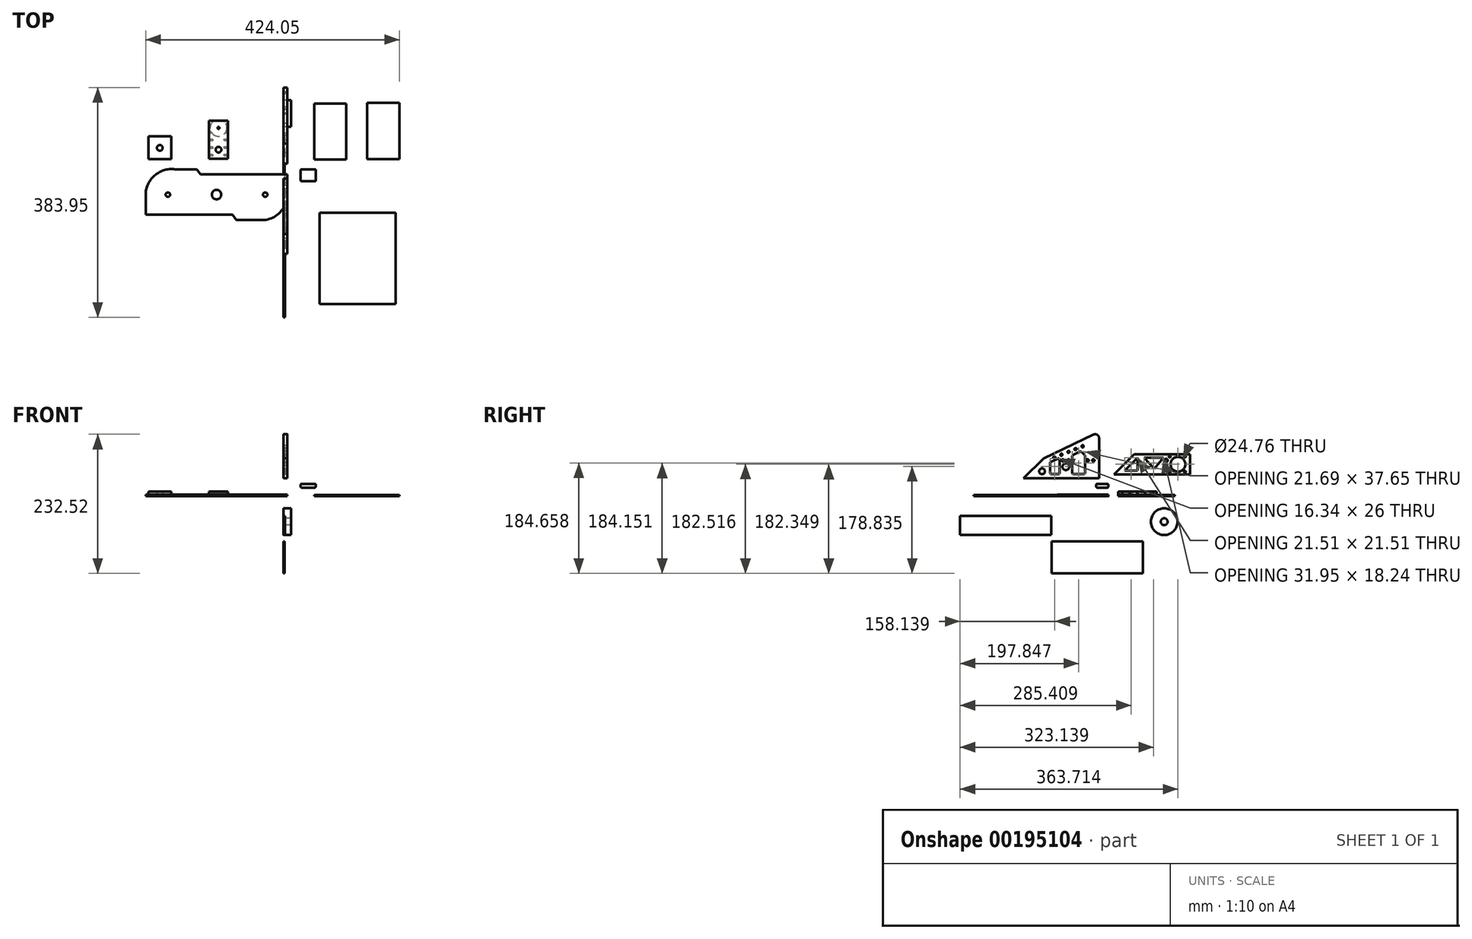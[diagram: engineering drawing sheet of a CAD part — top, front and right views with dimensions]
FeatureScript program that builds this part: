
annotation { "Feature Type Name" : "Feature", "Feature Type Description" : "" }
export const myFeature = defineFeature(function(context is Context, id is Id, definition is map)
    precondition{}
    {
        {
            var Q0;
            Q0=qCreatedBy(makeId("Top.planeOp"),FACE);
            var sketch = newSketch(context, id + "F0", { "sketchPlane" : qUnion([Q0])});
            skLineSegment(sketch, "E0.bottom", {"start": v(-85.5, -8.64) * mm, "end": v(-138.32, -8.64) * mm});
            skLineSegment(sketch, "E0.top", {"start": v(-85.5, -75.95) * mm, "end": v(-138.32, -75.95) * mm});
            skPoint(sketch, "E0.middle", {"position": v(-111.9, -42.3) * mm});
            skLineSegment(sketch, "E1", {"start": v(-138.32, -8.64) * mm, "end": v(-144.93, 0) * mm});
            skLineSegment(sketch, "E2", {"start": v(-144.93, 0) * mm, "end": v(-181.5, 0) * mm});
            skLineSegment(sketch, "E3", {"start": v(-181.5, -75.95) * mm, "end": v(-230.27, -75.95) * mm});
            skLineSegment(sketch, "E4", {"start": v(-230.27, -75.95) * mm, "end": v(-230.27, -42.93) * mm});
            skArc(sketch, "E5", {"start": v(-181.5, 0) * mm, "mid": v(-215.59, -10.44) * mm, "end": v(-230.27, -42.93) * mm});
            skLineSegment(sketch, "E6", {"start": v(-111.9, -42.3) * mm, "end": v(-100.72, -42.3) * mm});
            skLineSegment(sketch, "E7", {"start": v(-111.9, -42.3) * mm, "end": v(-111.9, -49.73) * mm});
            skLineSegment(sketch, "E8.MirrorCS", {"start": v(-42.31, -8.64) * mm, "end": v(6.46, -8.64) * mm});
            skLineSegment(sketch, "E9.MirrorCS", {"start": v(6.46, -8.64) * mm, "end": v(6.46, -41.66) * mm});
            skArc(sketch, "E10.MirrorCS", {"start": v(-42.31, -84.58) * mm, "mid": v(-8.23, -74.14) * mm, "end": v(6.46, -41.66) * mm});
            skLineSegment(sketch, "E11.MirrorCS", {"start": v(-78.89, -84.58) * mm, "end": v(-42.31, -84.58) * mm});
            skLineSegment(sketch, "E12.MirrorCS", {"start": v(-85.5, -75.95) * mm, "end": v(-78.89, -84.58) * mm});
            skLineSegment(sketch, "E13", {"start": v(-42.31, -8.64) * mm, "end": v(-85.5, -8.64) * mm});
            skLineSegment(sketch, "E14", {"start": v(-181.5, -75.95) * mm, "end": v(-138.32, -75.95) * mm});
            skCircle(sketch, "E15", {"center": v(-111.9, -42.3) * mm, "radius": 7.87 * mm});
            skCircle(sketch, "E16", {"center": v(-193.19, -42.3) * mm, "radius": 3.68 * mm});
            skCircle(sketch, "E17.MirrorC", {"center": v(-30.63, -42.3) * mm, "radius": 3.68 * mm});
            skSolve(sketch);
        }
        {
            var Q0;
            Q0 = qSketchRegion(id + "F0", true);
            extrude(context, id + "F1", {"entities" : qUnion([Q0]), "depth" : 3.05 * mm});
        }
        {
            var Q0;
            Q0=qCreatedBy(makeId("Top.planeOp"),FACE);
            var sketch = newSketch(context, id + "F2", { "sketchPlane" : qUnion([Q0])});
            skLineSegment(sketch, "E18.bottom", {"start": v(-187.63, 16.69) * mm, "end": v(-225.73, 16.69) * mm});
            skLineSegment(sketch, "E18.top", {"start": v(-187.63, 54.79) * mm, "end": v(-225.73, 54.79) * mm});
            skLineSegment(sketch, "E18.left", {"start": v(-187.63, 16.69) * mm, "end": v(-187.63, 54.79) * mm});
            skLineSegment(sketch, "E18.right", {"start": v(-225.73, 16.69) * mm, "end": v(-225.73, 54.79) * mm});
            skCircle(sketch, "E19", {"center": v(-206.68, 35.74) * mm, "radius": 4.76 * mm});
            skPoint(sketch, "E19.centerSnap0", {"position": v(-206.68, 54.79) * mm});
            skPoint(sketch, "E19.centerSnap1", {"position": v(-187.63, 35.74) * mm});
            skSolve(sketch);
        }
        {
            var Q0;
            Q0 = qSketchRegion(id + "F2", true);
            extrude(context, id + "F3", {"entities" : qUnion([Q0]), "depth" : 7.94 * mm});
        }
        {
            var Q0;
            Q0=qCreatedBy(makeId("Right.planeOp"),FACE);
            var sketch = newSketch(context, id + "F4", { "sketchPlane" : qUnion([Q0])});
            skLineSegment(sketch, "E20", {"start": v(-108.08, 63.04) * mm, "end": v(-24.5, 102.95) * mm});
            skLineSegment(sketch, "E21", {"start": v(-15.41, 97.22) * mm, "end": v(-15.41, 29.83) * mm});
            skLineSegment(sketch, "E22", {"start": v(-15.41, 29.83) * mm, "end": v(-106.33, 29.83) * mm});
            skLineSegment(sketch, "E23", {"start": v(-97.35, 54.98) * mm, "end": v(-97.35, 39.42) * mm});
            skLineSegment(sketch, "E24", {"start": v(-94.81, 36.88) * mm, "end": v(-83.55, 36.88) * mm});
            skLineSegment(sketch, "E25", {"start": v(-81.01, 39.42) * mm, "end": v(-81.01, 60.35) * mm});
            skLineSegment(sketch, "E26", {"start": v(-84.65, 62.64) * mm, "end": v(-95.9, 57.27) * mm});
            skCircle(sketch, "E27", {"center": v(-70.88, 49.3) * mm, "radius": 5.61 * mm});
            skLineSegment(sketch, "E28.direction1", {"start": v(-70.88, 49.3) * mm, "end": v(-43.02, 60.8) * mm, "construction": true});
            skLineSegment(sketch, "E28.direction2", {"start": v(-70.88, 49.3) * mm, "end": v(-70.88, 30.25) * mm, "construction": true});
            skLineSegment(sketch, "E29", {"start": v(-60.32, 66.48) * mm, "end": v(-60.32, 39.42) * mm});
            skLineSegment(sketch, "E30", {"start": v(-57.78, 36.88) * mm, "end": v(-41.17, 36.88) * mm});
            skLineSegment(sketch, "E31", {"start": v(-38.63, 39.42) * mm, "end": v(-38.63, 67.02) * mm});
            skLineSegment(sketch, "E32", {"start": v(-39.39, 68.83) * mm, "end": v(-44.45, 73.8) * mm});
            skLineSegment(sketch, "E33", {"start": v(-47.32, 74.28) * mm, "end": v(-58.87, 68.77) * mm});
            skLineSegment(sketch, "E34", {"start": v(-106.33, 29.83) * mm, "end": v(-141.28, 29.83) * mm});
            skLineSegment(sketch, "E35", {"start": v(-141.28, 29.83) * mm, "end": v(-108.08, 63.04) * mm});
            skCircle(sketch, "E36", {"center": v(-110.57, 41.64) * mm, "radius": 4.84 * mm});
            skPoint(sketch, "E37.visualSharp", {"position": v(-15.41, 107.28) * mm});
            skArc(sketch, "E37.filletArc", {"start": v(-15.41, 97.22) * mm, "mid": v(-18.37, 102.59) * mm, "end": v(-24.5, 102.95) * mm});
            skPoint(sketch, "E38.visualSharp", {"position": v(-45.71, 75.05) * mm});
            skArc(sketch, "E38.filletArc", {"start": v(-44.45, 73.8) * mm, "mid": v(-45.8, 74.5) * mm, "end": v(-47.32, 74.28) * mm});
            skPoint(sketch, "E39.visualSharp", {"position": v(-60.32, 68.08) * mm});
            skArc(sketch, "E39.filletArc", {"start": v(-58.87, 68.77) * mm, "mid": v(-59.92, 67.83) * mm, "end": v(-60.32, 66.48) * mm});
            skPoint(sketch, "E40.visualSharp", {"position": v(-38.63, 68.08) * mm});
            skArc(sketch, "E40.filletArc", {"start": v(-38.63, 67.02) * mm, "mid": v(-38.83, 68) * mm, "end": v(-39.39, 68.83) * mm});
            skPoint(sketch, "E41.visualSharp", {"position": v(-81.01, 64.38) * mm});
            skArc(sketch, "E41.filletArc", {"start": v(-81.01, 60.35) * mm, "mid": v(-82.2, 62.5) * mm, "end": v(-84.65, 62.64) * mm});
            skPoint(sketch, "E42.visualSharp", {"position": v(-97.35, 56.58) * mm});
            skArc(sketch, "E42.filletArc", {"start": v(-95.9, 57.27) * mm, "mid": v(-96.96, 56.33) * mm, "end": v(-97.35, 54.98) * mm});
            skPoint(sketch, "E43.visualSharp", {"position": v(-38.63, 36.88) * mm});
            skArc(sketch, "E43.filletArc", {"start": v(-41.17, 36.88) * mm, "mid": v(-39.37, 37.63) * mm, "end": v(-38.63, 39.42) * mm});
            skPoint(sketch, "E44.visualSharp", {"position": v(-60.32, 36.88) * mm});
            skArc(sketch, "E44.filletArc", {"start": v(-60.32, 39.42) * mm, "mid": v(-59.57, 37.63) * mm, "end": v(-57.78, 36.88) * mm});
            skPoint(sketch, "E45.visualSharp", {"position": v(-81.01, 36.88) * mm});
            skArc(sketch, "E45.filletArc", {"start": v(-83.55, 36.88) * mm, "mid": v(-81.76, 37.63) * mm, "end": v(-81.01, 39.42) * mm});
            skPoint(sketch, "E46.visualSharp", {"position": v(-97.35, 36.88) * mm});
            skArc(sketch, "E46.filletArc", {"start": v(-97.35, 39.42) * mm, "mid": v(-96.6, 37.63) * mm, "end": v(-94.81, 36.88) * mm});
            skCircle(sketch, "E47", {"center": v(-75.68, 59.86) * mm, "radius": 1.9 * mm});
            skCircle(sketch, "E48.1.0.0", {"center": v(-66.15, 59.86) * mm, "radius": 1.9 * mm});
            skLineSegment(sketch, "E48.direction1", {"start": v(-75.68, 59.86) * mm, "end": v(-66.15, 59.86) * mm, "construction": true});
            skPoint(sketch, "E49.middle", {"position": v(-70.92, 59.86) * mm});
            skCircle(sketch, "E50", {"center": v(-34.44, 59.86) * mm, "radius": 1.9 * mm});
            skCircle(sketch, "E51.1.0.0", {"center": v(-24.91, 59.86) * mm, "radius": 1.9 * mm});
            skSolve(sketch);
        }
        {
            var Q0;
            Q0 = qSketchRegion(id + "F4", true);
            extrude(context, id + "F5", {"entities" : qUnion([Q0]), "depth" : 6.35 * mm});
        }
        {
            var Q0;
            Q0=qCreatedBy(makeId("Top.planeOp"),FACE);
            var sketch = newSketch(context, id + "F6", { "sketchPlane" : qUnion([Q0])});
            skLineSegment(sketch, "E52.bottom", {"start": v(-124.5, 17.33) * mm, "end": v(-92.76, 17.33) * mm});
            skLineSegment(sketch, "E52.top", {"start": v(-124.5, 80.83) * mm, "end": v(-92.76, 80.83) * mm});
            skLineSegment(sketch, "E52.left", {"start": v(-124.5, 17.33) * mm, "end": v(-124.5, 80.83) * mm});
            skLineSegment(sketch, "E52.right", {"start": v(-92.76, 17.33) * mm, "end": v(-92.76, 80.83) * mm});
            skCircle(sketch, "E53", {"center": v(-108.63, 32.7) * mm, "radius": 4.76 * mm});
            skPoint(sketch, "E53.centerSnap0", {"position": v(-108.63, 17.33) * mm});
            skCircle(sketch, "E54", {"center": v(-108.63, 69.02) * mm, "radius": 1.65 * mm});
            skPoint(sketch, "E54.centerSnap0", {"position": v(-108.63, 80.83) * mm});
            skSolve(sketch);
        }
        {
            var Q0;
            Q0 = qSketchRegion(id + "F6", true);
            extrude(context, id + "F7", {"entities" : qUnion([Q0]), "depth" : 7.94 * mm});
        }
        {
            var Q0;
            Q0=makeQuery(id+"F7.opExtrude","SWEPT_FACE",FACE,{"disambiguationData":[OSD([sQuery(id+"F6.wireOp",EDGE,"E52.right")])]});
            var sketch = newSketch(context, id + "F8", { "sketchPlane" : qUnion([Q0])});
            skCircle(sketch, "E55", {"center": v(23.75, 3.97) * mm, "radius": 1.3 * mm});
            skPoint(sketch, "E55.centerSnap0", {"position": v(17.33, 3.97) * mm});
            skCircle(sketch, "E56.1.0.0", {"center": v(36.45, 3.97) * mm, "radius": 1.3 * mm});
            skCircle(sketch, "E56.2.0.0", {"center": v(49.15, 3.97) * mm, "radius": 1.3 * mm});
            skCircle(sketch, "E56.3.0.0", {"center": v(61.85, 3.97) * mm, "radius": 1.3 * mm});
            skCircle(sketch, "E56.4.0.0", {"center": v(74.55, 3.97) * mm, "radius": 1.3 * mm});
            skLineSegment(sketch, "E56.direction1", {"start": v(23.75, 3.97) * mm, "end": v(36.45, 3.97) * mm, "construction": true});
            skSolve(sketch);
        }
        {
            var Q0;
            Q0 = qSketchRegion(id + "F8", true);
            extrude(context, id + "F9", {"entities" : qUnion([Q0]), "operationType" : NewBodyOperationType.REMOVE, "oppositeDirection" : true, "depth" : 6.35 * mm});
        }
        {
            var Q0;
            Q0=makeQuery(id+"F7.opExtrude","SWEPT_FACE",FACE,{"disambiguationData":[OSD([sQuery(id+"F6.wireOp",EDGE,"E52.left")])]});
            var sketch = newSketch(context, id + "F10", { "sketchPlane" : qUnion([Q0])});
            skCircle(sketch, "E57", {"center": v(-23.1, 3.97) * mm, "radius": 1.36 * mm});
            skPoint(sketch, "E57.centerSnap0", {"position": v(-17.33, 3.97) * mm});
            skCircle(sketch, "E58.1.0.0", {"center": v(-35.8, 3.97) * mm, "radius": 1.36 * mm});
            skCircle(sketch, "E58.2.0.0", {"center": v(-48.5, 3.97) * mm, "radius": 1.36 * mm});
            skCircle(sketch, "E58.3.0.0", {"center": v(-61.2, 3.97) * mm, "radius": 1.36 * mm});
            skCircle(sketch, "E58.4.0.0", {"center": v(-73.9, 3.97) * mm, "radius": 1.36 * mm});
            skLineSegment(sketch, "E58.direction1", {"start": v(-23.1, 3.97) * mm, "end": v(-35.8, 3.97) * mm, "construction": true});
            skSolve(sketch);
        }
        {
            var Q0;
            Q0 = qSketchRegion(id + "F10", true);
            extrude(context, id + "F11", {"entities" : qUnion([Q0]), "operationType" : NewBodyOperationType.REMOVE, "oppositeDirection" : true, "depth" : 6.35 * mm});
        }
        {
            var Q0;
            Q0=makeQuery(id+"F5.opExtrude","CAP_FACE",FACE,{"disambiguationData":[OSD([sQuery(id+"F4.wireOp",EDGE,"hSpsFszO-E8va-vhgR-9E20-GIKQw1AIUSDn"),sQuery(id+"F4.wireOp",EDGE,"E20"),sQuery(id+"F4.wireOp",EDGE,"shNWkFX5-DmJ1-Q3tj-PIuK-kCnUBTTVJkQP"),sQuery(id+"F4.wireOp",EDGE,"E21"),sQuery(id+"F4.wireOp",EDGE,"E22"),sQuery(id+"F4.wireOp",EDGE,"E23"),sQuery(id+"F4.wireOp",EDGE,"E24"),sQuery(id+"F4.wireOp",EDGE,"E25"),sQuery(id+"F4.wireOp",EDGE,"E26"),sQuery(id+"F4.wireOp",EDGE,"E27"),sQuery(id+"F4.wireOp",EDGE,"E28.0.1.0"),sQuery(id+"F4.wireOp",EDGE,"E29"),sQuery(id+"F4.wireOp",EDGE,"E30"),sQuery(id+"F4.wireOp",EDGE,"E31"),sQuery(id+"F4.wireOp",EDGE,"E32"),sQuery(id+"F4.wireOp",EDGE,"E33"),sQuery(id+"F4.wireOp",EDGE,"JjvghidZ-4DsB-nMtc-syiM-kJHiGhE1ZNjx")])],"isStart":false});
            var sketch = newSketch(context, id + "F12", { "sketchPlane" : qUnion([Q0])});
            skCircle(sketch, "E59", {"center": v(-42.83, 83.43) * mm, "radius": 1.78 * mm});
            skCircle(sketch, "E60.1.0.0", {"center": v(-54.64, 78.75) * mm, "radius": 1.78 * mm});
            skCircle(sketch, "E60.2.0.0", {"center": v(-66.44, 74.07) * mm, "radius": 1.78 * mm});
            skCircle(sketch, "E60.3.0.0", {"center": v(-78.25, 69.38) * mm, "radius": 1.78 * mm});
            skCircle(sketch, "E60.4.0.0", {"center": v(-90.05, 64.7) * mm, "radius": 1.78 * mm});
            skLineSegment(sketch, "E60.direction1", {"start": v(-42.83, 83.43) * mm, "end": v(-54.64, 78.75) * mm, "construction": true});
            skSolve(sketch);
        }
        {
            var Q0;
            Q0 = qSketchRegion(id + "F12", true);
            var Q1;
            Q1 = qConstructionFilter(qBodyType(qCreatedBy(id + "F12" ,EDGE), BodyType.WIRE), ConstructionObject.NO);
            extrude(context, id + "F13", {"entities" : qUnion([Q0]), "operationType" : NewBodyOperationType.REMOVE, "surfaceEntities" : qUnion([Q1]), "endBound" : BoundingType.THROUGH_ALL, "oppositeDirection" : true, "depth" : 25.4 * mm});
        }
        {
            var Q0;
            Q0=makeQuery(id+"F7.opExtrude","CAP_FACE",FACE,{"disambiguationData":[OSD([sQuery(id+"F6.wireOp",EDGE,"E52.bottom"),sQuery(id+"F6.wireOp",EDGE,"E52.top"),sQuery(id+"F6.wireOp",EDGE,"E52.left"),sQuery(id+"F6.wireOp",EDGE,"E52.right"),sQuery(id+"F6.wireOp",EDGE,"E53"),sQuery(id+"F6.wireOp",EDGE,"E54")])],"isStart":true});
            var sketch = newSketch(context, id + "F14", { "sketchPlane" : qUnion([Q0])});
            skCircle(sketch, "E61", {"center": v(-108.63, -69.02) * mm, "radius": 14 * mm});
            skSolve(sketch);
        }
        {
            var Q0;
            Q0 = qSketchRegion(id + "F14", true);
            extrude(context, id + "F15", {"entities" : qUnion([Q0]), "operationType" : NewBodyOperationType.REMOVE, "oppositeDirection" : true, "depth" : 6.1 * mm});
        }
        {
            var Q0;
            Q0=qCreatedBy(makeId("Front.planeOp"),FACE);
            var sketch = newSketch(context, id + "F16", { "sketchPlane" : qUnion([Q0])});
            skLineSegment(sketch, "E62.bottom", {"start": v(28.64, 14.36) * mm, "end": v(53.64, 14.36) * mm});
            skLineSegment(sketch, "E62.top", {"start": v(28.64, 20.86) * mm, "end": v(53.64, 20.86) * mm});
            skLineSegment(sketch, "E62.left", {"start": v(28.64, 14.36) * mm, "end": v(28.64, 20.86) * mm});
            skLineSegment(sketch, "E62.right", {"start": v(53.64, 14.36) * mm, "end": v(53.64, 20.86) * mm});
            skSolve(sketch);
        }
        {
            var Q0;
            Q0 = qSketchRegion(id + "F16", true);
            extrude(context, id + "F17", {"entities" : qUnion([Q0]), "depth" : 20 * mm});
        }
        {
            var Q0;
            Q0=makeQuery(id+"F17.opExtrude","SWEPT_EDGE",EDGE,{"disambiguationData":[OSD([sQuery(id+"F16.wireOp",EDGE,"E62.top"),sQuery(id+"F16.wireOp",EDGE,"E62.right")])]});
            var Q1;
            Q1=makeQuery(id+"F17.opExtrude","SWEPT_EDGE",EDGE,{"disambiguationData":[OSD([sQuery(id+"F16.wireOp",EDGE,"E62.bottom"),sQuery(id+"F16.wireOp",EDGE,"E62.right")])]});
            var Q2;
            Q2=makeQuery(id+"F17.opExtrude","CAP_EDGE",EDGE,{"disambiguationData":[OSD([sQuery(id+"F16.wireOp",EDGE,"E62.right")])],"isStart":false});
            var Q3;
            Q3=makeQuery(id+"F17.opExtrude","CAP_EDGE",EDGE,{"disambiguationData":[OSD([sQuery(id+"F16.wireOp",EDGE,"E62.right")])],"isStart":true});
            var Q4;
            Q4=makeQuery(id+"F17.opExtrude","CAP_EDGE",EDGE,{"disambiguationData":[OSD([sQuery(id+"F16.wireOp",EDGE,"E62.top")])],"isStart":false});
            var Q5;
            Q5=makeQuery(id+"F17.opExtrude","CAP_EDGE",EDGE,{"disambiguationData":[OSD([sQuery(id+"F16.wireOp",EDGE,"E62.bottom")])],"isStart":false});
            var Q6;
            Q6=makeQuery(id+"F17.opExtrude","CAP_EDGE",EDGE,{"disambiguationData":[OSD([sQuery(id+"F16.wireOp",EDGE,"E62.top")])],"isStart":true});
            var Q7;
            Q7=makeQuery(id+"F17.opExtrude","CAP_EDGE",EDGE,{"disambiguationData":[OSD([sQuery(id+"F16.wireOp",EDGE,"E62.bottom")])],"isStart":true});
            var Q8;
            Q8=makeQuery(id+"F17.opExtrude","SWEPT_EDGE",EDGE,{"disambiguationData":[OSD([sQuery(id+"F16.wireOp",EDGE,"E62.top"),sQuery(id+"F16.wireOp",EDGE,"E62.left")])]});
            var Q9;
            Q9=makeQuery(id+"F17.opExtrude","CAP_EDGE",EDGE,{"disambiguationData":[OSD([sQuery(id+"F16.wireOp",EDGE,"E62.left")])],"isStart":true});
            var Q10;
            Q10=makeQuery(id+"F17.opExtrude","SWEPT_EDGE",EDGE,{"disambiguationData":[OSD([sQuery(id+"F16.wireOp",EDGE,"E62.bottom"),sQuery(id+"F16.wireOp",EDGE,"E62.left")])]});
            var Q11;
            Q11=makeQuery(id+"F17.opExtrude","CAP_EDGE",EDGE,{"disambiguationData":[OSD([sQuery(id+"F16.wireOp",EDGE,"E62.left")])],"isStart":false});
            fillet(context, id + "F18", {"entities" : qUnion([Q0, Q1, Q2, Q3, Q4, Q5, Q6, Q7, Q8, Q9, Q10, Q11]), "radius" : 1.65 * mm, "tangentPropagation" : true, "allowEdgeOverflow" : false});
        }
        {
            var Q0;
            Q0=qCreatedBy(makeId("Right.planeOp"),FACE);
            var sketch = newSketch(context, id + "F19", { "sketchPlane" : qUnion([Q0])});
            skLineSegment(sketch, "E63", {"start": v(136.63, 70.09) * mm, "end": v(136.63, 36.71) * mm});
            skLineSegment(sketch, "E64", {"start": v(136.63, 36.71) * mm, "end": v(9.63, 36.71) * mm});
            skLineSegment(sketch, "E65", {"start": v(9.63, 36.71) * mm, "end": v(43, 70.09) * mm});
            skLineSegment(sketch, "E66", {"start": v(43, 70.09) * mm, "end": v(136.63, 70.09) * mm});
            skLineSegment(sketch, "E67", {"start": v(76.71, 46.08) * mm, "end": v(59.84, 64.32) * mm});
            skLineSegment(sketch, "E68", {"start": v(59.84, 64.32) * mm, "end": v(91.8, 64.32) * mm});
            skLineSegment(sketch, "E69", {"start": v(91.8, 64.32) * mm, "end": v(76.71, 46.08) * mm});
            skPoint(sketch, "E70.centerSnap0", {"position": v(136.63, 53.4) * mm});
            skCircle(sketch, "E71", {"center": v(116.4, 53.4) * mm, "radius": 12.38 * mm});
            skCircle(sketch, "E72", {"center": v(96.46, 59.66) * mm, "radius": 2.77 * mm});
            skCircle(sketch, "E73.0.1.0", {"center": v(96.46, 47.47) * mm, "radius": 2.77 * mm});
            skLineSegment(sketch, "E73.direction1", {"start": v(96.46, 59.66) * mm, "end": v(121.86, 59.66) * mm, "construction": true});
            skLineSegment(sketch, "E73.direction2", {"start": v(96.46, 59.66) * mm, "end": v(96.46, 47.47) * mm, "construction": true});
            skCircle(sketch, "E74", {"center": v(102.63, 66.3) * mm, "radius": 1.59 * mm});
            skCircle(sketch, "E75.0.1.0", {"center": v(102.63, 40.9) * mm, "radius": 1.59 * mm});
            skCircle(sketch, "E75.1.0.0", {"center": v(128.03, 66.3) * mm, "radius": 1.59 * mm});
            skCircle(sketch, "E75.1.1.0", {"center": v(128.03, 40.9) * mm, "radius": 1.59 * mm});
            skLineSegment(sketch, "E75.direction1", {"start": v(102.63, 66.3) * mm, "end": v(128.03, 66.3) * mm, "construction": true});
            skLineSegment(sketch, "E75.direction2", {"start": v(102.63, 66.3) * mm, "end": v(102.63, 40.9) * mm, "construction": true});
            skCircle(sketch, "E76", {"center": v(58.3, 53.4) * mm, "radius": 1.59 * mm});
            skPoint(sketch, "E76.centerSnap0", {"position": v(26.32, 53.4) * mm});
            skLineSegment(sketch, "E77", {"start": v(48.84, 64.32) * mm, "end": v(48.84, 42.81) * mm});
            skLineSegment(sketch, "E78", {"start": v(48.84, 42.81) * mm, "end": v(27.33, 42.81) * mm});
            skLineSegment(sketch, "E79", {"start": v(48.84, 64.32) * mm, "end": v(27.33, 42.81) * mm});
            skSolve(sketch);
        }
        {
            var Q0;
            Q0=makeQuery(id+"F19.imprint","IMPRINT",FACE,{"disambiguationData":[TD([[makeQuery(id+"F19.imprint","IMPRINT",EDGE,{"derivedFrom":sQuery(id+"F19.wireOp",EDGE,"E63")}),-1.0]])]});
            extrude(context, id + "F20", {"entities" : qUnion([Q0]), "depth" : 6.35 * mm});
        }
        {
            var Q0;
            Q0=qCreatedBy(makeId("Right.planeOp"),FACE);
            var sketch = newSketch(context, id + "F21", { "sketchPlane" : qUnion([Q0])});
            skCircle(sketch, "E80", {"center": v(93.39, -42.46) * mm, "radius": 22.23 * mm});
            skCircle(sketch, "E81", {"center": v(93.39, -42.46) * mm, "radius": 5.72 * mm});
            skSolve(sketch);
        }
        {
            var Q0;
            Q0 = qSketchRegion(id + "F21", true);
            extrude(context, id + "F22", {"entities" : qUnion([Q0]), "depth" : 12.7 * mm});
        }
        {
            var Q0;
            Q0=qCreatedBy(makeId("Right.planeOp"),FACE);
            var sketch = newSketch(context, id + "F23", { "sketchPlane" : qUnion([Q0])});
            skLineSegment(sketch, "E82.bottom", {"start": v(-94.92, -32.78) * mm, "end": v(-247.32, -32.78) * mm});
            skLineSegment(sketch, "E82.top", {"start": v(-94.92, -64.53) * mm, "end": v(-247.32, -64.53) * mm});
            skLineSegment(sketch, "E82.left", {"start": v(-94.92, -32.78) * mm, "end": v(-94.92, -64.53) * mm});
            skLineSegment(sketch, "E82.right", {"start": v(-247.32, -32.78) * mm, "end": v(-247.32, -64.53) * mm});
            skPoint(sketch, "E82.middle", {"position": v(-171.12, -48.65) * mm});
            skSolve(sketch);
        }
        {
            var Q0;
            Q0 = qSketchRegion(id + "F23", true);
            extrude(context, id + "F24", {"entities" : qUnion([Q0]), "depth" : 2.3 * mm});
        }
        {
            var Q0;
            Q0=qCreatedBy(makeId("Top.planeOp"),FACE);
            var sketch = newSketch(context, id + "F25", { "sketchPlane" : qUnion([Q0])});
            skLineSegment(sketch, "E83.bottom", {"start": v(60.23, -72.5) * mm, "end": v(187.23, -72.5) * mm});
            skLineSegment(sketch, "E83.top", {"start": v(60.23, -224.9) * mm, "end": v(187.23, -224.9) * mm});
            skLineSegment(sketch, "E83.left", {"start": v(60.23, -72.5) * mm, "end": v(60.23, -224.9) * mm});
            skLineSegment(sketch, "E83.right", {"start": v(187.23, -72.5) * mm, "end": v(187.23, -224.9) * mm});
            skSolve(sketch);
        }
        {
            var Q0;
            Q0 = qSketchRegion(id + "F25", true);
            extrude(context, id + "F26", {"entities" : qUnion([Q0]), "depth" : 2.3 * mm});
        }
        {
            var Q0;
            Q0=qCreatedBy(makeId("Top.planeOp"),FACE);
            var sketch = newSketch(context, id + "F27", { "sketchPlane" : qUnion([Q0])});
            skLineSegment(sketch, "E84", {"start": v(51.3, 109.98) * mm, "end": v(104.78, 109.98) * mm});
            skLineSegment(sketch, "E85", {"start": v(104.78, 109.98) * mm, "end": v(104.78, 16.35) * mm});
            skLineSegment(sketch, "E86", {"start": v(104.78, 16.35) * mm, "end": v(51.3, 16.35) * mm});
            skLineSegment(sketch, "E87", {"start": v(51.3, 16.35) * mm, "end": v(51.3, 109.98) * mm});
            skSolve(sketch);
        }
        {
            var Q0;
            Q0 = qSketchRegion(id + "F27", true);
            extrude(context, id + "F28", {"entities" : qUnion([Q0]), "depth" : 2.3 * mm});
        }
        {
            var Q0;
            Q0=qCreatedBy(makeId("Top.planeOp"),FACE);
            var sketch = newSketch(context, id + "F29", { "sketchPlane" : qUnion([Q0])});
            skLineSegment(sketch, "E88.bottom", {"start": v(139.3, 17.24) * mm, "end": v(193.78, 17.24) * mm});
            skLineSegment(sketch, "E88.top", {"start": v(139.3, 110.87) * mm, "end": v(193.78, 110.87) * mm});
            skLineSegment(sketch, "E88.left", {"start": v(139.3, 17.24) * mm, "end": v(139.3, 110.87) * mm});
            skLineSegment(sketch, "E88.right", {"start": v(193.78, 17.24) * mm, "end": v(193.78, 110.87) * mm});
            skSolve(sketch);
        }
        {
            var Q0;
            Q0 = qSketchRegion(id + "F29", true);
            extrude(context, id + "F30", {"entities" : qUnion([Q0]), "depth" : 2.3 * mm});
        }
        {
            var Q0;
            Q0=qCreatedBy(makeId("Right.planeOp"),FACE);
            var sketch = newSketch(context, id + "F31", { "sketchPlane" : qUnion([Q0])});
            skLineSegment(sketch, "E89.bottom", {"start": v(58.06, -128.95) * mm, "end": v(-94.34, -128.95) * mm});
            skLineSegment(sketch, "E89.top", {"start": v(58.06, -75.6) * mm, "end": v(-94.34, -75.6) * mm});
            skLineSegment(sketch, "E89.left", {"start": v(58.06, -128.95) * mm, "end": v(58.06, -75.6) * mm});
            skLineSegment(sketch, "E89.right", {"start": v(-94.34, -128.95) * mm, "end": v(-94.34, -75.6) * mm});
            skSolve(sketch);
        }
        {
            var Q0;
            Q0 = qSketchRegion(id + "F31", true);
            extrude(context, id + "F32", {"entities" : qUnion([Q0]), "depth" : 1.6 * mm});
        }
    });
